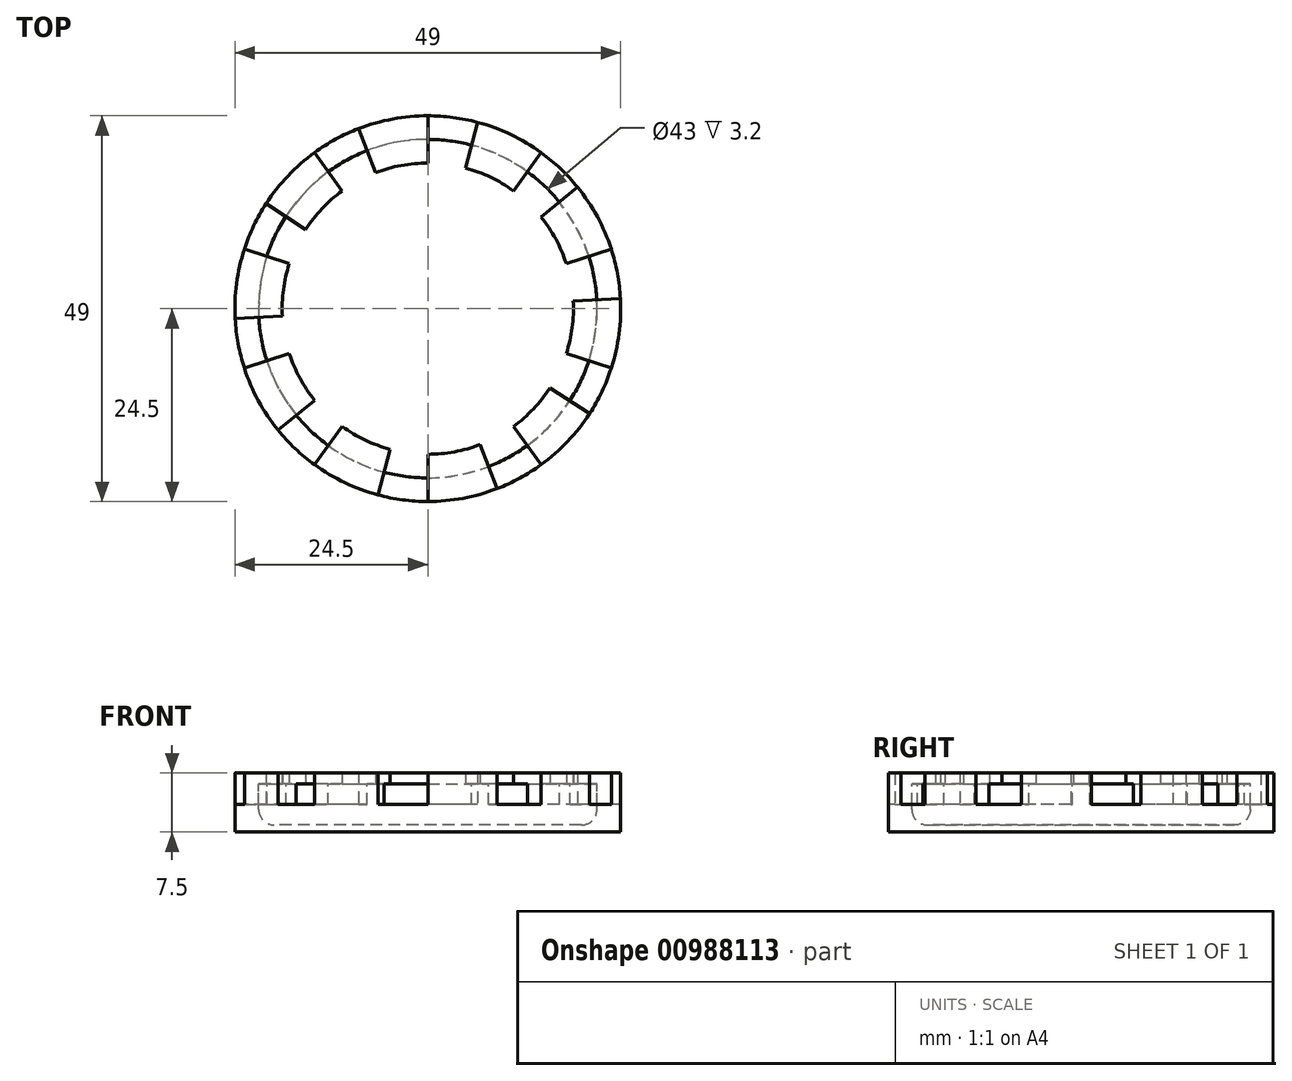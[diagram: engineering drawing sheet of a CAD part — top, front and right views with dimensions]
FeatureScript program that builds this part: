
annotation { "Feature Type Name" : "Feature", "Feature Type Description" : "" }
export const myFeature = defineFeature(function(context is Context, id is Id, definition is map)
    precondition{}
    {
        {
            var Q0;
            Q0=qCreatedBy(makeId("Top.planeOp"),FACE);
            var sketch = newSketch(context, id + "F0", { "sketchPlane" : qUnion([Q0])});
            skCircle(sketch, "E0", {"center": v(0, 0) * mm, "radius": 24.5 * mm});
            skSolve(sketch);
        }
        {
            var Q0;
            Q0 = qSketchRegion(id + "F0", true);
            extrude(context, id + "F1", {"entities" : qUnion([Q0]), "depth" : 7.5 * mm, "offsetDistance" : 25 * mm});
        }
        {
            var Q0;
            Q0=makeQuery(id+"F1.opExtrude","CAP_FACE",FACE,{"disambiguationData":[OSD([sQuery(id+"F0.wireOp",EDGE,"E0")])],"isStart":false});
            var sketch = newSketch(context, id + "F2", { "sketchPlane" : qUnion([Q0])});
            skCircle(sketch, "E1", {"center": v(0, 0) * mm, "radius": 21.5 * mm});
            skSolve(sketch);
        }
        {
            var Q0;
            Q0 = qSketchRegion(id + "F2", true);
            extrude(context, id + "F3", {"entities" : qUnion([Q0]), "operationType" : NewBodyOperationType.REMOVE, "oppositeDirection" : true, "depth" : 6.6 * mm, "offsetDistance" : 25 * mm});
        }
        {
            var Q0;
            Q0=makeQuery(id+"F3.boolean.opBoolean","COPY",FACE,{"derivedFrom":makeQuery(id+"F3.opExtrude","CAP_FACE",FACE,{"disambiguationData":[OSD([sQuery(id+"F2.wireOp",EDGE,"E1")])],"isStart":false})});
            cPlane(context, id + "F4", {"entities" : qUnion([Q0]), "cplaneType" : CPlaneType.OFFSET, "offset" : 5.2 * mm, "width" : 150 * mm, "height" : 150 * mm});
        }
        {
            var Q0;
            Q0=qCreatedBy(id+"F4.planeOp",FACE);
            var sketch = newSketch(context, id + "F5", { "sketchPlane" : qUnion([Q0])});
            skCircle(sketch, "E2.0", {"center": v(0, 0) * mm, "radius": 21.5 * mm});
            skCircle(sketch, "E3", {"center": v(0, 0) * mm, "radius": 18.5 * mm});
            skSolve(sketch);
        }
        {
            var Q0;
            Q0 = qSketchRegion(id + "F5", true);
            var Q1;
            Q1=makeQuery(id+"F1.opExtrude","CAP_FACE",FACE,{"disambiguationData":[OSD([sQuery(id+"F0.wireOp",EDGE,"E0")])],"isStart":false});
            extrude(context, id + "F6", {"entities" : qUnion([Q0]), "operationType" : NewBodyOperationType.ADD, "endBound" : BoundingType.UP_TO_SURFACE, "depth" : 25 * mm, "endBoundEntityFace" : qUnion([Q1]), "offsetDistance" : 25 * mm});
        }
        {
            var Q0;
            Q0=makeQuery(id+"F6.boolean.opBoolean","MERGE",FACE,{"derivedFrom":[makeQuery(id+"F1.opExtrude","CAP_FACE",FACE,{"disambiguationData":[OSD([sQuery(id+"F0.wireOp",EDGE,"E0")])],"isStart":false}),makeQuery(id+"F6.opExtrude","CAP_FACE",FACE,{"disambiguationData":[OSD([sQuery(id+"F5.wireOp",EDGE,"E2.0"),sQuery(id+"F5.wireOp",EDGE,"E3")])],"isStart":false})]});
            var sketch = newSketch(context, id + "F7", { "sketchPlane" : qUnion([Q0])});
            skLineSegment(sketch, "E4", {"start": v(0, 0) * mm, "end": v(0, 27.14) * mm});
            skLineSegment(sketch, "E5", {"start": v(0, 27.14) * mm, "end": v(7.27, 27.14) * mm});
            skLineSegment(sketch, "E6", {"start": v(7.27, 27.14) * mm, "end": v(0, 0) * mm});
            skLineSegment(sketch, "E7.1.0", {"start": v(0, 0) * mm, "end": v(-15.95, 21.96) * mm});
            skLineSegment(sketch, "E7.1.1", {"start": v(-15.95, 21.96) * mm, "end": v(-10.07, 26.23) * mm});
            skLineSegment(sketch, "E7.1.2", {"start": v(-10.07, 26.23) * mm, "end": v(0, 0) * mm});
            skLineSegment(sketch, "E7.2.0", {"start": v(0, 0) * mm, "end": v(-25.81, 8.39) * mm});
            skLineSegment(sketch, "E7.2.1", {"start": v(-25.81, 8.39) * mm, "end": v(-23.57, 15.3) * mm});
            skLineSegment(sketch, "E7.2.2", {"start": v(-23.57, 15.3) * mm, "end": v(0, 0) * mm});
            skLineSegment(sketch, "E7.3.0", {"start": v(0, 0) * mm, "end": v(-25.81, -8.39) * mm});
            skLineSegment(sketch, "E7.3.1", {"start": v(-25.81, -8.39) * mm, "end": v(-28.06, -1.47) * mm});
            skLineSegment(sketch, "E7.3.2", {"start": v(-28.06, -1.47) * mm, "end": v(0, 0) * mm});
            skLineSegment(sketch, "E7.4.0", {"start": v(0, 0) * mm, "end": v(-15.95, -21.96) * mm});
            skLineSegment(sketch, "E7.4.1", {"start": v(-15.95, -21.96) * mm, "end": v(-21.84, -17.68) * mm});
            skLineSegment(sketch, "E7.4.2", {"start": v(-21.84, -17.68) * mm, "end": v(0, 0) * mm});
            skLineSegment(sketch, "E7.5.0", {"start": v(0, 0) * mm, "end": v(0, -27.14) * mm});
            skLineSegment(sketch, "E7.5.1", {"start": v(0, -27.14) * mm, "end": v(-7.27, -27.14) * mm});
            skLineSegment(sketch, "E7.5.2", {"start": v(-7.27, -27.14) * mm, "end": v(0, 0) * mm});
            skLineSegment(sketch, "E7.6.0", {"start": v(0, 0) * mm, "end": v(15.95, -21.96) * mm});
            skLineSegment(sketch, "E7.6.1", {"start": v(15.95, -21.96) * mm, "end": v(10.07, -26.23) * mm});
            skLineSegment(sketch, "E7.6.2", {"start": v(10.07, -26.23) * mm, "end": v(0, 0) * mm});
            skLineSegment(sketch, "E7.7.0", {"start": v(0, 0) * mm, "end": v(25.81, -8.39) * mm});
            skLineSegment(sketch, "E7.7.1", {"start": v(25.81, -8.39) * mm, "end": v(23.57, -15.3) * mm});
            skLineSegment(sketch, "E7.7.2", {"start": v(23.57, -15.3) * mm, "end": v(0, 0) * mm});
            skLineSegment(sketch, "E7.8.0", {"start": v(0, 0) * mm, "end": v(25.81, 8.39) * mm});
            skLineSegment(sketch, "E7.8.1", {"start": v(25.81, 8.39) * mm, "end": v(28.06, 1.47) * mm});
            skLineSegment(sketch, "E7.8.2", {"start": v(28.06, 1.47) * mm, "end": v(0, 0) * mm});
            skLineSegment(sketch, "E7.9.0", {"start": v(0, 0) * mm, "end": v(15.95, 21.96) * mm});
            skLineSegment(sketch, "E7.9.1", {"start": v(15.95, 21.96) * mm, "end": v(21.84, 17.68) * mm});
            skLineSegment(sketch, "E7.9.2", {"start": v(21.84, 17.68) * mm, "end": v(0, 0) * mm});
            skPoint(sketch, "E7.center", {"position": v(0, 0) * mm});
            skSolve(sketch);
        }
        {
            var Q0;
            Q0 = qSketchRegion(id + "F7", true);
            extrude(context, id + "F8", {"entities" : qUnion([Q0]), "operationType" : NewBodyOperationType.REMOVE, "oppositeDirection" : true, "depth" : 4 * mm, "offsetDistance" : 25 * mm});
        }
        {
            var Q0;
            Q0=makeQuery(id+"F3.boolean.opBoolean","COPY",EDGE,{"derivedFrom":makeQuery(id+"F3.opExtrude","CAP_EDGE",EDGE,{"disambiguationData":[OSD([sQuery(id+"F2.wireOp",EDGE,"E1")])],"isStart":false})});
            fillet(context, id + "F9", {"entities" : qUnion([Q0]), "tangentPropagation" : true, "radius" : 2 * mm, "defaultsChanged" : true, "vertexSettings" : [], "allowEdgeOverflow" : false});
        }
    });
